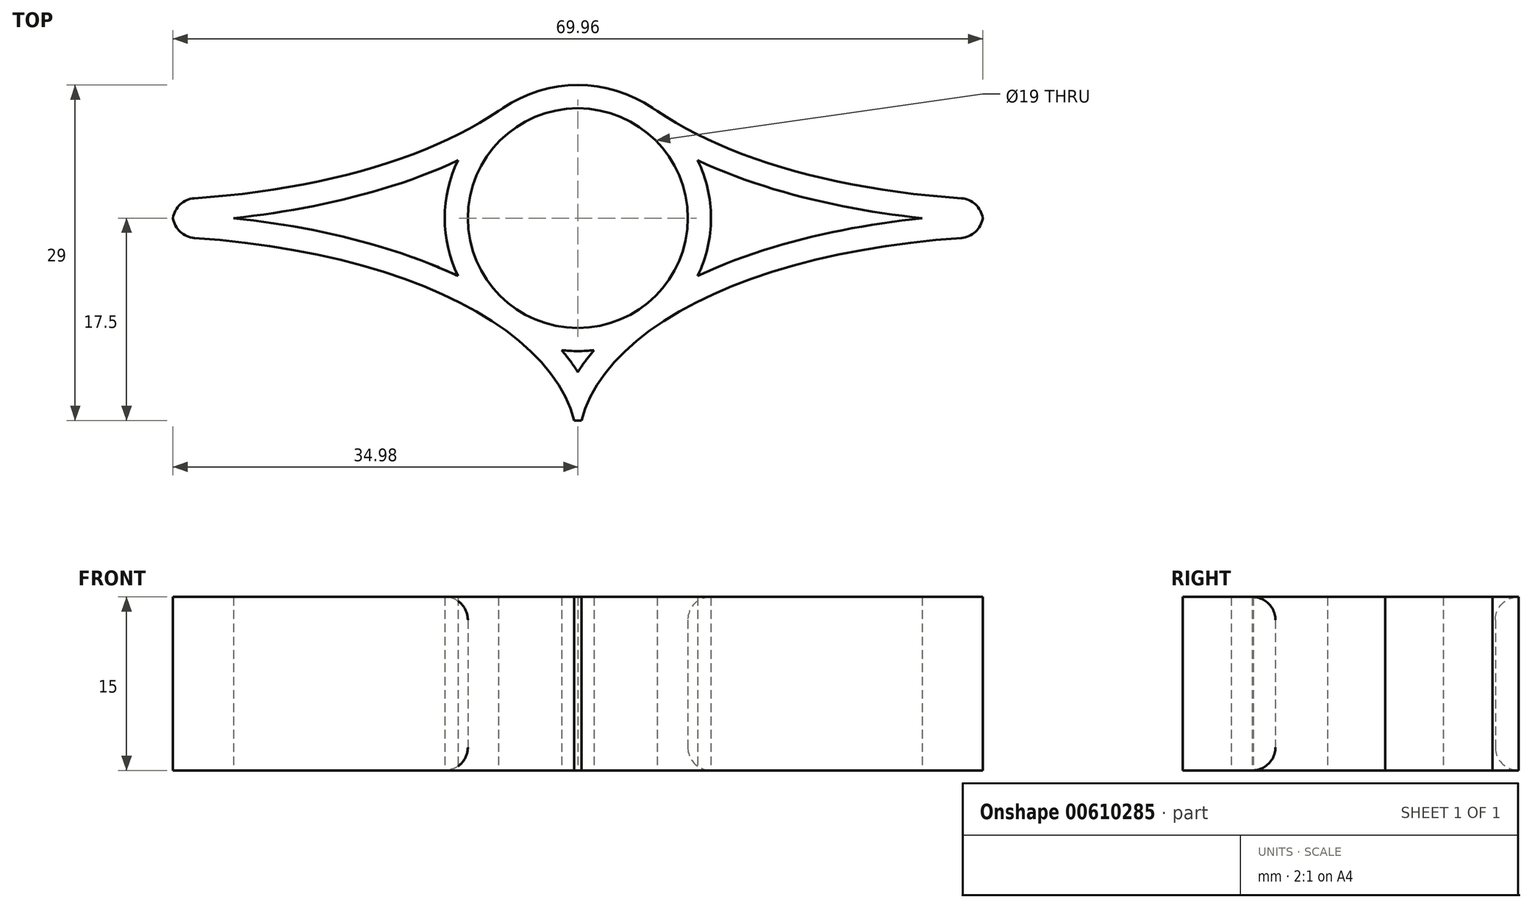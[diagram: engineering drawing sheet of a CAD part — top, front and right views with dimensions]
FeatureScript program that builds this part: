
annotation { "Feature Type Name" : "Feature", "Feature Type Description" : "" }
export const myFeature = defineFeature(function(context is Context, id is Id, definition is map)
    precondition{}
    {
        {
            var Q0;
            Q0=qCreatedBy(makeId("Top.planeOp"),FACE);
            var sketch = newSketch(context, id + "F0", { "sketchPlane" : qUnion([Q0])});
            skCircle(sketch, "E0", {"center": v(0, 0) * mm, "radius": 9.5 * mm});
            skLineSegment(sketch, "E1.bottom", {"start": v(35, 17.5) * mm, "end": v(-35, 17.5) * mm});
            skLineSegment(sketch, "E1.top", {"start": v(35, -17.5) * mm, "end": v(-35, -17.5) * mm});
            skLineSegment(sketch, "E1.left", {"start": v(35, 17.5) * mm, "end": v(35, -17.5) * mm});
            skLineSegment(sketch, "E1.right", {"start": v(-35, 17.5) * mm, "end": v(-35, -17.5) * mm});
            skSolve(sketch);
        }
        {
            var Q0;
            Q0=makeQuery(id+"F0.imprint","IMPRINT",FACE,{"disambiguationData":[TD([[makeQuery(id+"F0.imprint","IMPRINT",EDGE,{"derivedFrom":sQuery(id+"F0.wireOp",EDGE,"E0")}),-1.0]])]});
            extrude(context, id + "F1", {"entities" : qUnion([Q0]), "endBound" : BoundingType.SYMMETRIC, "depth" : 15 * mm, "offsetDistance" : 25 * mm});
        }
        {
            var Q0;
            Q0=qCreatedBy(makeId("Top.planeOp"),FACE);
            var sketch = newSketch(context, id + "F2", { "sketchPlane" : qUnion([Q0])});
            skEllipse(sketch, "E2", {"center": v(-43.64, 22) * mm, "majorRadius": 43.7 * mm, "minorRadius": 20.36 * mm, "majorAxis": v(1, -0.06)});
            skLineSegment(sketch, "E3", {"start": v(0, 40.21) * mm, "end": v(0, -28.46) * mm});
            skLineSegment(sketch, "E4", {"start": v(-56.45, 0) * mm, "end": v(53.65, 0) * mm});
            skEllipse(sketch, "E5.MirrorC", {"center": v(43.64, 22) * mm, "majorRadius": 43.7 * mm, "minorRadius": 20.36 * mm, "majorAxis": v(-1, -0.06)});
            skEllipse(sketch, "E6.MirrorC", {"center": v(43.64, -22) * mm, "majorRadius": 43.7 * mm, "minorRadius": 20.36 * mm, "majorAxis": v(-1, 0.06)});
            skEllipse(sketch, "E7.MirrorC", {"center": v(-43.64, -22) * mm, "majorRadius": 43.7 * mm, "minorRadius": 20.36 * mm, "majorAxis": v(1, 0.06)});
            skSolve(sketch);
        }
        {
            var Q0;
            Q0=makeQuery(id+"F2.imprint","IMPRINT",FACE,{"disambiguationData":[TD([[makeQuery(id+"F2.imprint","IMPRINT",EDGE,{"derivedFrom":sQuery(id+"F2.wireOp",EDGE,"E2")}),1.0]])]});
            var Q1;
            Q1=makeQuery(id+"F2.imprint","IMPRINT",FACE,{"disambiguationData":[TD([[makeQuery(id+"F2.imprint","IMPRINT",EDGE,{"derivedFrom":sQuery(id+"F2.wireOp",EDGE,"E5.MirrorC")}),1.0]])]});
            var Q2;
            Q2=makeQuery(id+"F2.imprint","IMPRINT",FACE,{"disambiguationData":[TD([[makeQuery(id+"F2.imprint","IMPRINT",EDGE,{"derivedFrom":sQuery(id+"F2.wireOp",EDGE,"E6.MirrorC")}),1.0]])]});
            var Q3;
            Q3=makeQuery(id+"F2.imprint","IMPRINT",FACE,{"disambiguationData":[TD([[makeQuery(id+"F2.imprint","IMPRINT",EDGE,{"derivedFrom":sQuery(id+"F2.wireOp",EDGE,"E7.MirrorC")}),1.0]])]});
            extrude(context, id + "F3", {"entities" : qUnion([Q0, Q1, Q2, Q3]), "operationType" : NewBodyOperationType.REMOVE, "endBound" : BoundingType.SYMMETRIC, "depth" : 25 * mm, "offsetDistance" : 25 * mm});
        }
        {
            var Q0;
            Q0=makeQuery(id+"F1.opExtrude","CAP_FACE",FACE,{"disambiguationData":[OSD([sQuery(id+"F0.wireOp",EDGE,"E0"),sQuery(id+"F0.wireOp",EDGE,"E1.bottom"),sQuery(id+"F0.wireOp",EDGE,"E1.top"),sQuery(id+"F0.wireOp",EDGE,"E1.left"),sQuery(id+"F0.wireOp",EDGE,"E1.right")])],"isStart":false});
            var Q1;
            Q1=makeQuery(id+"F1.opExtrude","CAP_FACE",FACE,{"disambiguationData":[OSD([sQuery(id+"F0.wireOp",EDGE,"E0"),sQuery(id+"F0.wireOp",EDGE,"E1.bottom"),sQuery(id+"F0.wireOp",EDGE,"E1.top"),sQuery(id+"F0.wireOp",EDGE,"E1.left"),sQuery(id+"F0.wireOp",EDGE,"E1.right")])],"isStart":true});
            shell(context, id + "F4", {"entities" : qUnion([Q0, Q1]), "thickness" : 2 * mm});
        }
        {
            var Q0;
            Q0=makeQuery(id+"F1.opExtrude","CAP_EDGE",EDGE,{"disambiguationData":[OSD([sQuery(id+"F0.wireOp",EDGE,"E0")])],"isStart":false});
            var Q1;
            Q1=makeQuery(id+"F1.opExtrude","CAP_EDGE",EDGE,{"disambiguationData":[OSD([sQuery(id+"F0.wireOp",EDGE,"E0")])],"isStart":true});
            fillet(context, id + "F5", {"entities" : qUnion([Q0, Q1]), "radius" : 2 * mm, "tangentPropagation" : true, "allowEdgeOverflow" : false});
        }
        {
            var Q0;
            Q0=makeQuery(id+"F3.boolean.opBoolean","INTERSECT",EDGE,{"derivedFrom":[makeQuery(id+"F1.opExtrude","SWEPT_FACE",FACE,{"disambiguationData":[OSD([sQuery(id+"F0.wireOp",EDGE,"E1.right")])]}),makeQuery(id+"F3.opExtrude","SWEPT_FACE",FACE,{"disambiguationData":[OSD([sQuery(id+"F2.wireOp",EDGE,"E2")])]})]});
            var Q1;
            Q1=makeQuery(id+"F3.boolean.opBoolean","INTERSECT",EDGE,{"derivedFrom":[makeQuery(id+"F1.opExtrude","SWEPT_FACE",FACE,{"disambiguationData":[OSD([sQuery(id+"F0.wireOp",EDGE,"E1.right")])]}),makeQuery(id+"F3.opExtrude","SWEPT_FACE",FACE,{"disambiguationData":[OSD([sQuery(id+"F2.wireOp",EDGE,"E7.MirrorC")])]})]});
            var Q2;
            Q2=makeQuery(id+"F3.boolean.opBoolean","INTERSECT",EDGE,{"derivedFrom":[makeQuery(id+"F1.opExtrude","SWEPT_FACE",FACE,{"disambiguationData":[OSD([sQuery(id+"F0.wireOp",EDGE,"E1.left")])]}),makeQuery(id+"F3.opExtrude","SWEPT_FACE",FACE,{"disambiguationData":[OSD([sQuery(id+"F2.wireOp",EDGE,"E5.MirrorC")])]})]});
            var Q3;
            Q3=makeQuery(id+"F3.boolean.opBoolean","INTERSECT",EDGE,{"derivedFrom":[makeQuery(id+"F1.opExtrude","SWEPT_FACE",FACE,{"disambiguationData":[OSD([sQuery(id+"F0.wireOp",EDGE,"E1.left")])]}),makeQuery(id+"F3.opExtrude","SWEPT_FACE",FACE,{"disambiguationData":[OSD([sQuery(id+"F2.wireOp",EDGE,"E6.MirrorC")])]})]});
            fillet(context, id + "F6", {"entities" : qUnion([Q0, Q1, Q2, Q3]), "radius" : 2 * mm, "tangentPropagation" : true, "allowEdgeOverflow" : false});
        }
        {
            var Q0;
            Q0=qCreatedBy(makeId("Top.planeOp"),FACE);
            var sketch = newSketch(context, id + "F7", { "sketchPlane" : qUnion([Q0])});
            skArc(sketch, "E8", {"start": v(6.8, 9.27) * mm, "mid": v(0, 11.5) * mm, "end": v(-6.8, 9.27) * mm});
            skArc(sketch, "E9", {"start": v(15.18, 9.27) * mm, "mid": v(0, 17.78) * mm, "end": v(-15.18, 9.27) * mm});
            skLineSegment(sketch, "E10", {"start": v(-15.18, 9.27) * mm, "end": v(-6.8, 9.27) * mm});
            skLineSegment(sketch, "E11.trimOffspring", {"start": v(6.8, 9.27) * mm, "end": v(15.18, 9.27) * mm});
            skSolve(sketch);
        }
        {
            var Q0;
            Q0 = qSketchRegion(id + "F7", true);
            extrude(context, id + "F8", {"entities" : qUnion([Q0]), "operationType" : NewBodyOperationType.REMOVE, "endBound" : BoundingType.SYMMETRIC, "oppositeDirection" : true, "depth" : 25 * mm, "offsetDistance" : 25 * mm});
        }
        {
            var Q0;
            Q0=makeQuery(id+"F8.boolean.opBoolean","COPY",EDGE,{"derivedFrom":makeQuery(id+"F8.opExtrude","SWEPT_EDGE",EDGE,{"disambiguationData":[OSD([sQuery(id+"F7.wireOp",EDGE,"E8"),sQuery(id+"F7.wireOp",EDGE,"E10")])]})});
            var Q1;
            Q1=makeQuery(id+"F8.boolean.opBoolean","COPY",EDGE,{"derivedFrom":makeQuery(id+"F8.opExtrude","SWEPT_EDGE",EDGE,{"disambiguationData":[OSD([sQuery(id+"F7.wireOp",EDGE,"E8"),sQuery(id+"F7.wireOp",EDGE,"E11.trimOffspring")])]})});
            fillet(context, id + "F9", {"entities" : qUnion([Q0, Q1]), "radius" : 5 * mm, "tangentPropagation" : true, "allowEdgeOverflow" : false});
        }
    });
